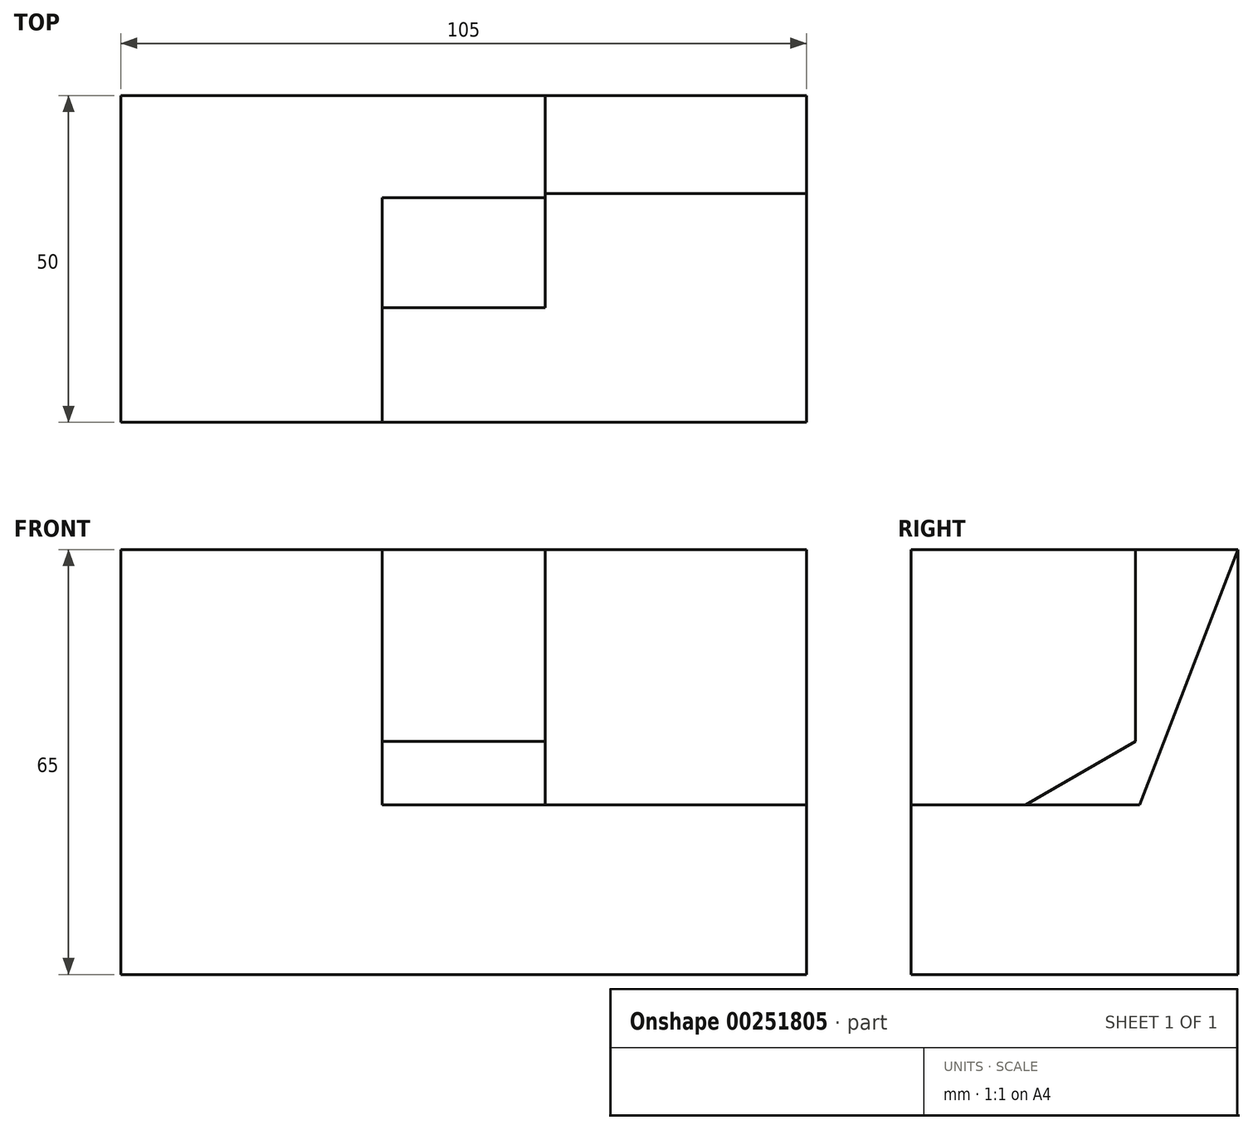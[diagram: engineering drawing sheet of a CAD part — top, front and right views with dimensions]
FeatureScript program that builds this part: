
annotation { "Feature Type Name" : "Feature", "Feature Type Description" : "" }
export const myFeature = defineFeature(function(context is Context, id is Id, definition is map)
    precondition{}
    {
        {
            var Q0;
            Q0=qCreatedBy(makeId("Front.planeOp"),FACE);
            var sketch = newSketch(context, id + "F0", { "sketchPlane" : qUnion([Q0])});
            skLineSegment(sketch, "E0.bottom", {"start": v(-52.5, 32.5) * mm, "end": v(52.5, 32.5) * mm});
            skLineSegment(sketch, "E0.top", {"start": v(-52.5, -32.5) * mm, "end": v(52.5, -32.5) * mm});
            skLineSegment(sketch, "E0.left", {"start": v(-52.5, 32.5) * mm, "end": v(-52.5, -32.5) * mm});
            skLineSegment(sketch, "E0.right", {"start": v(52.5, 32.5) * mm, "end": v(52.5, -32.5) * mm});
            skPoint(sketch, "E0.middle", {"position": v(0, 0) * mm});
            skSolve(sketch);
        }
        {
            var Q0;
            Q0 = qSketchRegion(id + "F0", true);
            extrude(context, id + "F1", {"entities" : qUnion([Q0]), "oppositeDirection" : true, "depth" : 50 * mm});
        }
        {
            var Q0;
            Q0=makeQuery(id+"F1.opExtrude","SWEPT_FACE",FACE,{"disambiguationData":[OSD([sQuery(id+"F0.wireOp",EDGE,"E0.right")])]});
            var sketch = newSketch(context, id + "F2", { "sketchPlane" : qUnion([Q0])});
            skLineSegment(sketch, "E1", {"start": v(0, -6.58) * mm, "end": v(35, -6.58) * mm});
            skLineSegment(sketch, "E2", {"start": v(35, -6.58) * mm, "end": v(50, 32.5) * mm});
            skSolve(sketch);
        }
        {
            var Q0;
            Q0 = qSketchRegion(id + "F2", true);
            var Q1;
            {var subQ0=sQuery(id+"F2.wireOp",EDGE,"E1");Q1=makeQuery(id+"F2.imprint","IMPRINT",FACE,{"disambiguationData":[TD([[makeQuery(id+"F2.imprint","IMPRINT",EDGE,{"derivedFrom":subQ0}),1.0]])]});}
            var Q2;
            Q2 = qSketchRegion(id + "F4", true);
            extrude(context, id + "F3", {"entities" : qUnion([Q0, Q1, Q2]), "operationType" : NewBodyOperationType.REMOVE, "oppositeDirection" : true, "depth" : 40 * mm});
        }
        {
            var Q0;
            Q0=makeQuery(id+"F3.boolean.opBoolean","COPY",FACE,{"derivedFrom":makeQuery(id+"F3.opExtrude","CAP_FACE",FACE,{"disambiguationData":[OSD([sQuery(id+"F0.wireOp",EDGE,"E0.bottom"),sQuery(id+"F0.wireOp",EDGE,"E0.right"),sQuery(id+"F2.wireOp",EDGE,"E1"),sQuery(id+"F2.wireOp",EDGE,"E2")])],"isStart":false})});
            var sketch = newSketch(context, id + "F4", { "sketchPlane" : qUnion([Q0])});
            skPoint(sketch, "E3.end.orphan", {"position": v(17.5, -6.58) * mm});
            skLineSegment(sketch, "E4", {"start": v(50, 32.5) * mm, "end": v(34.35, 32.5) * mm});
            skLineSegment(sketch, "E5", {"start": v(34.35, 32.5) * mm, "end": v(34.35, 3.15) * mm});
            skLineSegment(sketch, "E6", {"start": v(34.35, 3.15) * mm, "end": v(17.5, -6.58) * mm});
            skSolve(sketch);
        }
        {
            var Q0;
            Q0 = qSketchRegion(id + "F4", true);
            var Q1;
            {var subQ3=sQuery(id+"F4.wireOp",EDGE,"E5");Q1=makeQuery(id+"F4.imprint","IMPRINT",FACE,{"disambiguationData":[TD([[makeQuery(id+"F4.imprint","IMPRINT",EDGE,{"derivedFrom":subQ3}),-1.0]])]});}
            extrude(context, id + "F5", {"entities" : qUnion([Q0, Q1]), "operationType" : NewBodyOperationType.ADD, "oppositeDirection" : true, "depth" : 25 * mm});
        }
        {
            var Q0;
            {var subQ3=sQuery(id+"F4.wireOp",EDGE,"E5");Q0=makeQuery(id+"F4.imprint","IMPRINT",FACE,{"disambiguationData":[TD([[makeQuery(id+"F4.imprint","IMPRINT",EDGE,{"derivedFrom":subQ3}),-1.0]])]});}
            extrude(context, id + "F6", {"entities" : qUnion([Q0]), "operationType" : NewBodyOperationType.ADD, "oppositeDirection" : true, "depth" : 25 * mm});
        }
        {
            var Q0;
            {var subQ3=sQuery(id+"F4.wireOp",EDGE,"E5");Q0=makeQuery(id+"F4.imprint","IMPRINT",FACE,{"disambiguationData":[TD([[makeQuery(id+"F4.imprint","IMPRINT",EDGE,{"derivedFrom":subQ3}),-1.0]])]});}
            extrude(context, id + "F7", {"entities" : qUnion([Q0]), "operationType" : NewBodyOperationType.REMOVE, "oppositeDirection" : true, "depth" : 25 * mm});
        }
    });
